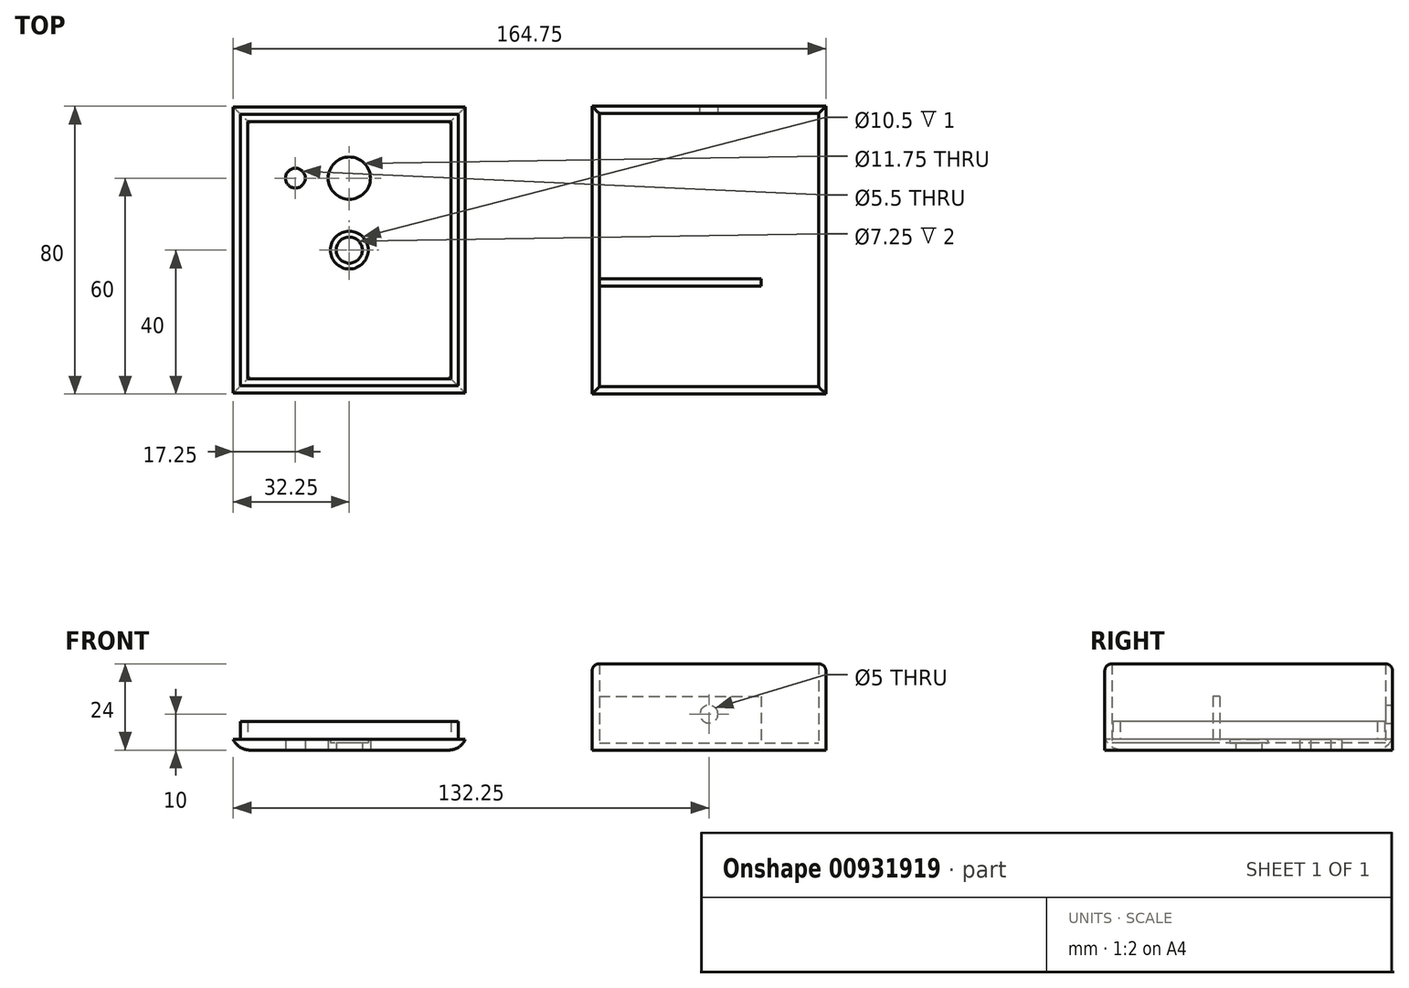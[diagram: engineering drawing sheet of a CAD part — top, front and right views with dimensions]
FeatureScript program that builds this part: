
annotation { "Feature Type Name" : "Feature", "Feature Type Description" : "" }
export const myFeature = defineFeature(function(context is Context, id is Id, definition is map)
    precondition{}
    {
        {
            var Q0;
            Q0=qCreatedBy(makeId("Top.planeOp"),FACE);
            var sketch = newSketch(context, id + "F0", { "sketchPlane" : qUnion([Q0])});
            skLineSegment(sketch, "E0.bottom", {"start": v(-32.5, 40) * mm, "end": v(32.5, 40) * mm});
            skLineSegment(sketch, "E0.top", {"start": v(-32.5, -40) * mm, "end": v(32.5, -40) * mm});
            skLineSegment(sketch, "E0.left", {"start": v(-32.5, 40) * mm, "end": v(-32.5, -40) * mm});
            skLineSegment(sketch, "E0.right", {"start": v(32.5, 40) * mm, "end": v(32.5, -40) * mm});
            skPoint(sketch, "E0.middle", {"position": v(0, 0) * mm});
            skLineSegment(sketch, "E1.0", {"start": v(-30.5, 38) * mm, "end": v(30.5, 38) * mm});
            skLineSegment(sketch, "E1.1", {"start": v(-30.5, 38) * mm, "end": v(-30.5, -38) * mm});
            skLineSegment(sketch, "E1.2", {"start": v(-30.5, -38) * mm, "end": v(30.5, -38) * mm});
            skLineSegment(sketch, "E1.3", {"start": v(30.5, 38) * mm, "end": v(30.5, -38) * mm});
            skLineSegment(sketch, "E2.bottom", {"start": v(-30.5, -8) * mm, "end": v(14.5, -8) * mm});
            skLineSegment(sketch, "E2.top", {"start": v(-30.5, -10) * mm, "end": v(14.5, -10) * mm});
            skLineSegment(sketch, "E2.left", {"start": v(-30.5, -8) * mm, "end": v(-30.5, -10) * mm});
            skLineSegment(sketch, "E2.right", {"start": v(14.5, -8) * mm, "end": v(14.5, -10) * mm});
            skLineSegment(sketch, "E3.bottom", {"start": v(-69.75, 37.75) * mm, "end": v(-130.25, 37.75) * mm});
            skLineSegment(sketch, "E3.top", {"start": v(-69.75, -37.75) * mm, "end": v(-130.25, -37.75) * mm});
            skLineSegment(sketch, "E3.left", {"start": v(-69.75, 37.75) * mm, "end": v(-69.75, -37.75) * mm});
            skLineSegment(sketch, "E3.right", {"start": v(-130.25, 37.75) * mm, "end": v(-130.25, -37.75) * mm});
            skPoint(sketch, "E3.middle", {"position": v(-100, 0) * mm});
            skLineSegment(sketch, "E4.0", {"start": v(-71.75, 35.75) * mm, "end": v(-71.75, -35.75) * mm});
            skLineSegment(sketch, "E4.1", {"start": v(-71.75, 35.75) * mm, "end": v(-128.25, 35.75) * mm});
            skLineSegment(sketch, "E4.2", {"start": v(-128.25, 35.75) * mm, "end": v(-128.25, -35.75) * mm});
            skLineSegment(sketch, "E4.3", {"start": v(-71.75, -35.75) * mm, "end": v(-128.25, -35.75) * mm});
            skLineSegment(sketch, "E5.0", {"start": v(-67.75, 39.75) * mm, "end": v(-67.75, -39.75) * mm});
            skLineSegment(sketch, "E5.1", {"start": v(-67.75, 39.75) * mm, "end": v(-132.25, 39.75) * mm});
            skLineSegment(sketch, "E5.2", {"start": v(-132.25, 39.75) * mm, "end": v(-132.25, -39.75) * mm});
            skLineSegment(sketch, "E5.3", {"start": v(-67.75, -39.75) * mm, "end": v(-132.25, -39.75) * mm});
            skCircle(sketch, "E6", {"center": v(-100, 20) * mm, "radius": 5.88 * mm});
            skCircle(sketch, "E7", {"center": v(-100, 0) * mm, "radius": 3.62 * mm});
            skCircle(sketch, "E8", {"center": v(-100, 0) * mm, "radius": 5.25 * mm});
            skCircle(sketch, "E9", {"center": v(-115, 20) * mm, "radius": 2.75 * mm});
            skSolve(sketch);
        }
        {
            var Q0;
            {var subQ4=sQuery(id+"F0.wireOp",EDGE,"E1.0");Q0=makeQuery(id+"F0.imprint","IMPRINT",FACE,{"disambiguationData":[TD([[makeQuery(id+"F0.imprint","IMPRINT",EDGE,{"derivedFrom":subQ4}),-1.0]])]});}
            extrude(context, id + "F1", {"entities" : qUnion([Q0]), "depth" : 2 * mm, "offsetDistance" : 25 * mm});
        }
        {
            var Q0;
            Q0=makeQuery(id+"F0.imprint","IMPRINT",FACE,{"disambiguationData":[TD([[makeQuery(id+"F0.imprint","IMPRINT",EDGE,{"derivedFrom":sQuery(id+"F0.wireOp",EDGE,"E0.bottom")}),-1.0]])]});
            extrude(context, id + "F2", {"entities" : qUnion([Q0]), "operationType" : NewBodyOperationType.ADD, "depth" : 24 * mm, "offsetDistance" : 25 * mm});
        }
        {
            var Q0;
            Q0=makeQuery(id+"F0.imprint","IMPRINT",FACE,{"disambiguationData":[TD([[makeQuery(id+"F0.imprint","IMPRINT",EDGE,{"derivedFrom":sQuery(id+"F0.wireOp",EDGE,"E2.bottom")}),-1.0]])]});
            extrude(context, id + "F3", {"entities" : qUnion([Q0]), "operationType" : NewBodyOperationType.ADD, "depth" : 15 * mm, "offsetDistance" : 25 * mm});
        }
        {
            var Q0;
            Q0=makeQuery(id+"F2.opExtrude","SWEPT_FACE",FACE,{"disambiguationData":[OSD([sQuery(id+"F0.wireOp",EDGE,"E0.bottom")])]});
            var sketch = newSketch(context, id + "F4", { "sketchPlane" : qUnion([Q0])});
            skCircle(sketch, "E10", {"center": v(0, 10) * mm, "radius": 2.5 * mm});
            skSolve(sketch);
        }
        {
            var Q0;
            Q0=makeQuery(id+"F4.imprint","IMPRINT",FACE,{"disambiguationData":[TD([[makeQuery(id+"F4.imprint","IMPRINT",EDGE,{"derivedFrom":sQuery(id+"F4.wireOp",EDGE,"E10")}),1.0]])]});
            var Q1;
            Q1=makeQuery(id+"F2.opExtrude","SWEPT_FACE",FACE,{"disambiguationData":[OSD([sQuery(id+"F0.wireOp",EDGE,"E1.0")])]});
            extrude(context, id + "F5", {"entities" : qUnion([Q0]), "operationType" : NewBodyOperationType.REMOVE, "endBound" : BoundingType.UP_TO_SURFACE, "oppositeDirection" : true, "depth" : 25 * mm, "endBoundEntityFace" : qUnion([Q1]), "offsetDistance" : 25 * mm});
        }
        {
            var Q0;
            Q0=makeQuery(id+"F2.opExtrude","CAP_EDGE",EDGE,{"disambiguationData":[OSD([sQuery(id+"F0.wireOp",EDGE,"E0.left")])],"isStart":false});
            var Q1;
            Q1=makeQuery(id+"F2.opExtrude","CAP_EDGE",EDGE,{"disambiguationData":[OSD([sQuery(id+"F0.wireOp",EDGE,"E0.bottom")])],"isStart":false});
            var Q2;
            Q2=makeQuery(id+"F2.opExtrude","CAP_EDGE",EDGE,{"disambiguationData":[OSD([sQuery(id+"F0.wireOp",EDGE,"E0.right")])],"isStart":false});
            var Q3;
            Q3=makeQuery(id+"F2.opExtrude","CAP_EDGE",EDGE,{"disambiguationData":[OSD([sQuery(id+"F0.wireOp",EDGE,"E0.top")])],"isStart":false});
            fillet(context, id + "F6", {"entities" : qUnion([Q0, Q1, Q2, Q3]), "radius" : 2 * mm, "tangentPropagation" : true, "allowEdgeOverflow" : false});
        }
        {
            var Q0;
            Q0=makeQuery(id+"F0.imprint","IMPRINT",FACE,{"disambiguationData":[TD([[makeQuery(id+"F0.imprint","IMPRINT",EDGE,{"derivedFrom":sQuery(id+"F0.wireOp",EDGE,"E3.bottom")}),-1.0]])]});
            var Q1;
            Q1=makeQuery(id+"F0.imprint","IMPRINT",FACE,{"disambiguationData":[TD([[makeQuery(id+"F0.imprint","IMPRINT",EDGE,{"derivedFrom":sQuery(id+"F0.wireOp",EDGE,"E4.0")}),-1.0]])]});
            extrude(context, id + "F7", {"entities" : qUnion([Q0, Q1]), "depth" : 3 * mm, "offsetDistance" : 25 * mm});
        }
        {
            var Q0;
            Q0=makeQuery(id+"F0.imprint","IMPRINT",FACE,{"disambiguationData":[TD([[makeQuery(id+"F0.imprint","IMPRINT",EDGE,{"derivedFrom":sQuery(id+"F0.wireOp",EDGE,"E3.bottom")}),1.0]])]});
            extrude(context, id + "F8", {"entities" : qUnion([Q0]), "operationType" : NewBodyOperationType.ADD, "depth" : 8 * mm, "offsetDistance" : 25 * mm});
        }
        {
            var Q0;
            Q0=makeQuery(id+"F0.imprint","IMPRINT",FACE,{"disambiguationData":[TD([[makeQuery(id+"F0.imprint","IMPRINT",EDGE,{"derivedFrom":sQuery(id+"F0.wireOp",EDGE,"E7")}),-1.0]])]});
            extrude(context, id + "F9", {"entities" : qUnion([Q0]), "operationType" : NewBodyOperationType.ADD, "depth" : 2 * mm, "offsetDistance" : 25 * mm});
        }
        {
            var Q0;
            Q0=makeQuery(id+"F7.opExtrude","CAP_EDGE",EDGE,{"disambiguationData":[OSD([sQuery(id+"F0.wireOp",EDGE,"E5.1")])],"isStart":true});
            var Q1;
            Q1=makeQuery(id+"F7.opExtrude","CAP_EDGE",EDGE,{"disambiguationData":[OSD([sQuery(id+"F0.wireOp",EDGE,"E5.2")])],"isStart":true});
            var Q2;
            Q2=makeQuery(id+"F7.opExtrude","CAP_EDGE",EDGE,{"disambiguationData":[OSD([sQuery(id+"F0.wireOp",EDGE,"E5.0")])],"isStart":true});
            var Q3;
            Q3=makeQuery(id+"F7.opExtrude","CAP_EDGE",EDGE,{"disambiguationData":[OSD([sQuery(id+"F0.wireOp",EDGE,"E5.3")])],"isStart":true});
            fillet(context, id + "F10", {"entities" : qUnion([Q0, Q1, Q2, Q3]), "radius" : 5 * mm, "tangentPropagation" : true, "allowEdgeOverflow" : false});
        }
    });
